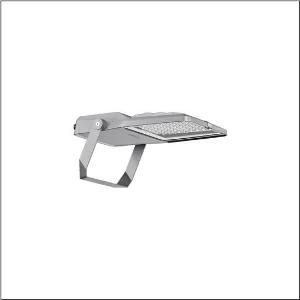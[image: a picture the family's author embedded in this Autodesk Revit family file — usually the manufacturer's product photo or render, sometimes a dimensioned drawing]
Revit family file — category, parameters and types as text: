
# Revit family: floodlight_fl_21_iq_mini___pl61_5xa7772b3c1a_b78d
name_source: partatom
category: Lighting Fixtures
units: mm (PartAtom-declared; Revit-internal decimal feet)

## family parameters
Cut with Voids When Loaded = No
Host = Face
Light Source = No
Part Type = Normal
Room Calculation Point = No
Round Connector Dimension = Use Diameter
Shared = No

## types (1)
- --- (1 x LED, 5270 lm, 45.5 W, 3000K)
    Apparent Load = 46 VA
    CIE Flux Codes = 33 65 98 100 100
    Color Rendering = 80
    Color Temperature = 3000K
    Default Elevation = 1800 mm
    Description = Floodlight FL 21 iQ mini, floodlight, primary light control with lens, of PMMA, primary optical cover: protective disc, of toughened safety glass, transparent, light distribution: PL61, light emission: direct distribution, installation type: surface-mounted, LED, High Power LED, rated luminous flux: 5.270lm, luminous efficacy: 116lm/W, light colour: 830, colour temperature: 3000K, control: Street-Remote, Auto-Match, Temp-Guard, Night-Set, Smart-Wire, Desk-Remote (wireless, voltage-free reading and setting of iQ features in the workshop via application-optimized NFC function/RFID function), optimised constant luminous flux control (CLO 2.0), with terminal, 6-pole, mains connection: 220..240V, AC, 50/60Hz, start of lifetime: 46W, end of service life: 48W, reduction: 21W, luminaire housing, of diecast aluminium, powder-coated, Siteco® metallic grey (DB 702S), corrosivity category C5 mid according to DIN EN ISO 12944, sealing non-destructively replaceable, mounting bracket, of steel, galvanised, powder-coated, Siteco® metallic grey (DB 702S), protection rating (complete): IP66, insulation class (complete): insulation class II (safety insulation), certification: CE, ENEC, VDE, protection symbol: D, impact resistance: IK08, permissible operating ambient temperature: -40..+40°C, permissible operating ambient temperature for outdoor applications: -40..+50°C, standard: DIN EN 12944, LABS conformity tested according to VDMA 24364:2018-05, packaging unit: 1 piece

Light Distribution: PL61
    Height = 70 mm
    Lamp = 1 x LED
    Lamp Light Flux = 5270 lm
    Lamp Power = 45.5 W
    Lamp count = 1
    Length = 485 mm
    Luminous efficacy = 116 lm/W
    Manufacturer = Siteco
    ModVariant = No
    Model = 5XA7772B3C1A
    Number of Poles = 1
    OnlyDefault = Yes
    Power Factor = 1
    Product Name = Floodlight FL 21 iQ mini | PL61
    Product group = floodlight | pylon annexe
    ProductGroupID = 6200
    Protection Class = Protection class II
    Protection Degree = IP 66
    RLX_Detail_Level = 1
    RLX_Emergency_Light_Flux = 0 lm
    RLX_Emergency_Type = 0
    RLX_Emergency_Type_DB = No
    RlxData = <blob elided: 96237 chars, md5=ed1df356>
    Socket = socket
    Standby Power = 0 W
    System Light Flux = 5270 lm
    System Power = 46 W
    Type Comments = factory setting: luminous flux: 100 % | dim-lin: 254 | 463 mA
    Type Image = l_1006845.jpg
    URL = http://relux.com
    VarID = @adj_106623
    Voltage = 0 V
    Weight = 0.00 kg
    Width = 337 mm

## geometry (parser evidence)
native form markers: Blend x4, Sweep x14
no freeform markers — native parametric forms only
